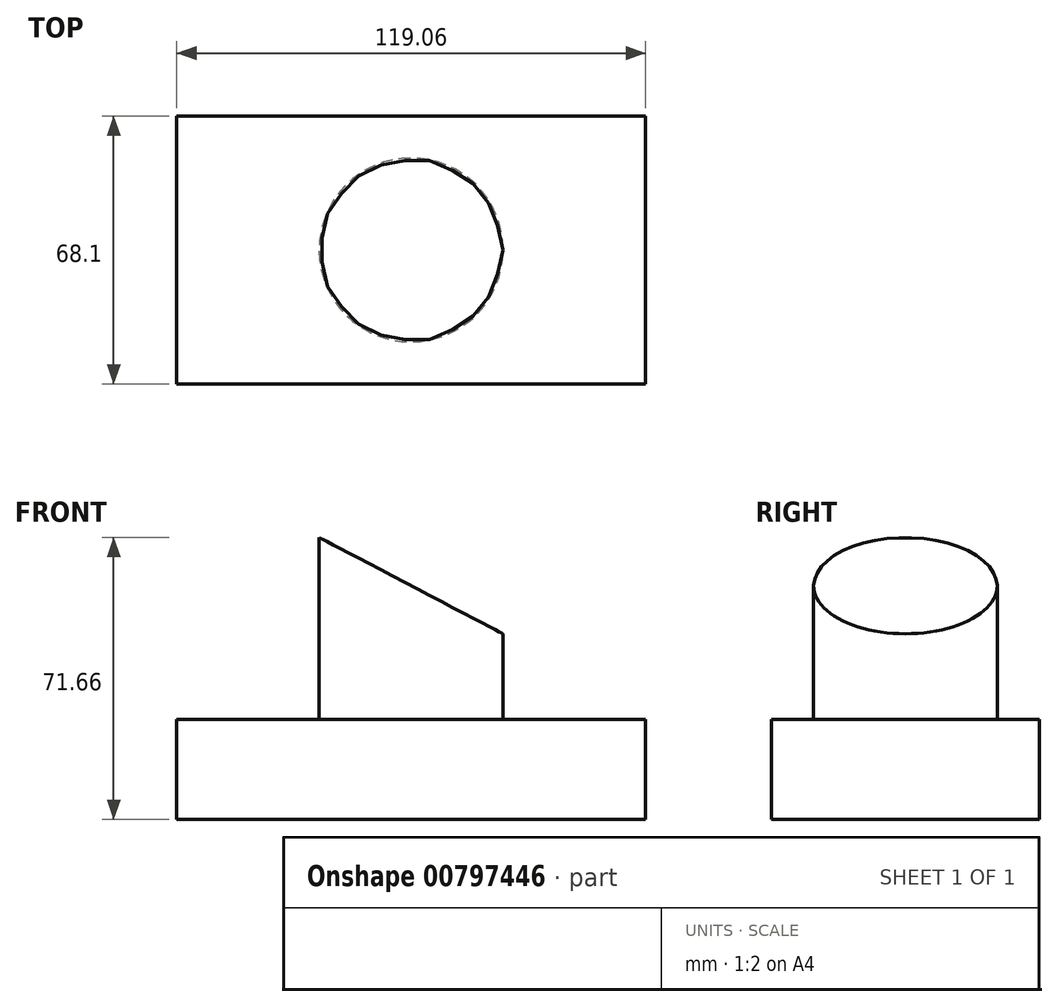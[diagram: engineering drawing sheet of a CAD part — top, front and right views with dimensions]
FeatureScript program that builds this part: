
annotation { "Feature Type Name" : "Feature", "Feature Type Description" : "" }
export const myFeature = defineFeature(function(context is Context, id is Id, definition is map)
    precondition{}
    {
        {
            var Q0;
            Q0=qCreatedBy(makeId("Top.planeOp"),FACE);
            var sketch = newSketch(context, id + "F0", { "sketchPlane" : qUnion([Q0])});
            skLineSegment(sketch, "E0.bottom", {"start": v(-59.53, 34.05) * mm, "end": v(59.53, 34.05) * mm});
            skLineSegment(sketch, "E0.top", {"start": v(-59.53, -34.05) * mm, "end": v(59.53, -34.05) * mm});
            skLineSegment(sketch, "E0.left", {"start": v(-59.53, 34.05) * mm, "end": v(-59.53, -34.05) * mm});
            skLineSegment(sketch, "E0.right", {"start": v(59.53, 34.05) * mm, "end": v(59.53, -34.05) * mm});
            skPoint(sketch, "E0.middle", {"position": v(0, 0) * mm});
            skSolve(sketch);
        }
        {
            var Q0;
            Q0 = qSketchRegion(id + "F0", true);
            extrude(context, id + "F1", {"entities" : qUnion([Q0]), "depth" : 25.4 * mm, "offsetDistance" : 25.4 * mm});
        }
        {
            var Q0;
            Q0=makeQuery(id+"F1.opExtrude","CAP_FACE",FACE,{"disambiguationData":[OSD([sQuery(id+"F0.wireOp",EDGE,"E0.bottom"),sQuery(id+"F0.wireOp",EDGE,"E0.top"),sQuery(id+"F0.wireOp",EDGE,"E0.left"),sQuery(id+"F0.wireOp",EDGE,"E0.right")])],"isStart":false});
            var sketch = newSketch(context, id + "F2", { "sketchPlane" : qUnion([Q0])});
            skCircle(sketch, "E1", {"center": v(0, 0) * mm, "radius": 23.34 * mm});
            skSolve(sketch);
        }
        {
            var Q0;
            Q0 = qSketchRegion(id + "F2", true);
            extrude(context, id + "F3", {"entities" : qUnion([Q0]), "operationType" : NewBodyOperationType.ADD, "depth" : 47.24 * mm, "offsetDistance" : 25.4 * mm});
        }
        {
            var Q0;
            Q0=qCreatedBy(makeId("Front.planeOp"),FACE);
            var sketch = newSketch(context, id + "F4", { "sketchPlane" : qUnion([Q0])});
            skLineSegment(sketch, "E2", {"start": v(-38.53, 79.63) * mm, "end": v(40.58, 38.15) * mm});
            skLineSegment(sketch, "E3", {"start": v(40.58, 38.15) * mm, "end": v(40.58, 78.35) * mm});
            skLineSegment(sketch, "E4", {"start": v(40.58, 78.35) * mm, "end": v(-36.1, 78.35) * mm});
            skSolve(sketch);
        }
        {
            var Q0;
            {var subQ0=sQuery(id+"F4.wireOp",EDGE,"E3");Q0=makeQuery(id+"F4.imprint","IMPRINT",FACE,{"disambiguationData":[TD([[makeQuery(id+"F4.imprint","IMPRINT",EDGE,{"derivedFrom":subQ0}),1.0]])]});}
            extrude(context, id + "F5", {"entities" : qUnion([Q0]), "operationType" : NewBodyOperationType.REMOVE, "endBound" : BoundingType.SYMMETRIC, "oppositeDirection" : true, "depth" : 65.02 * mm, "offsetDistance" : 25.4 * mm});
        }
    });
